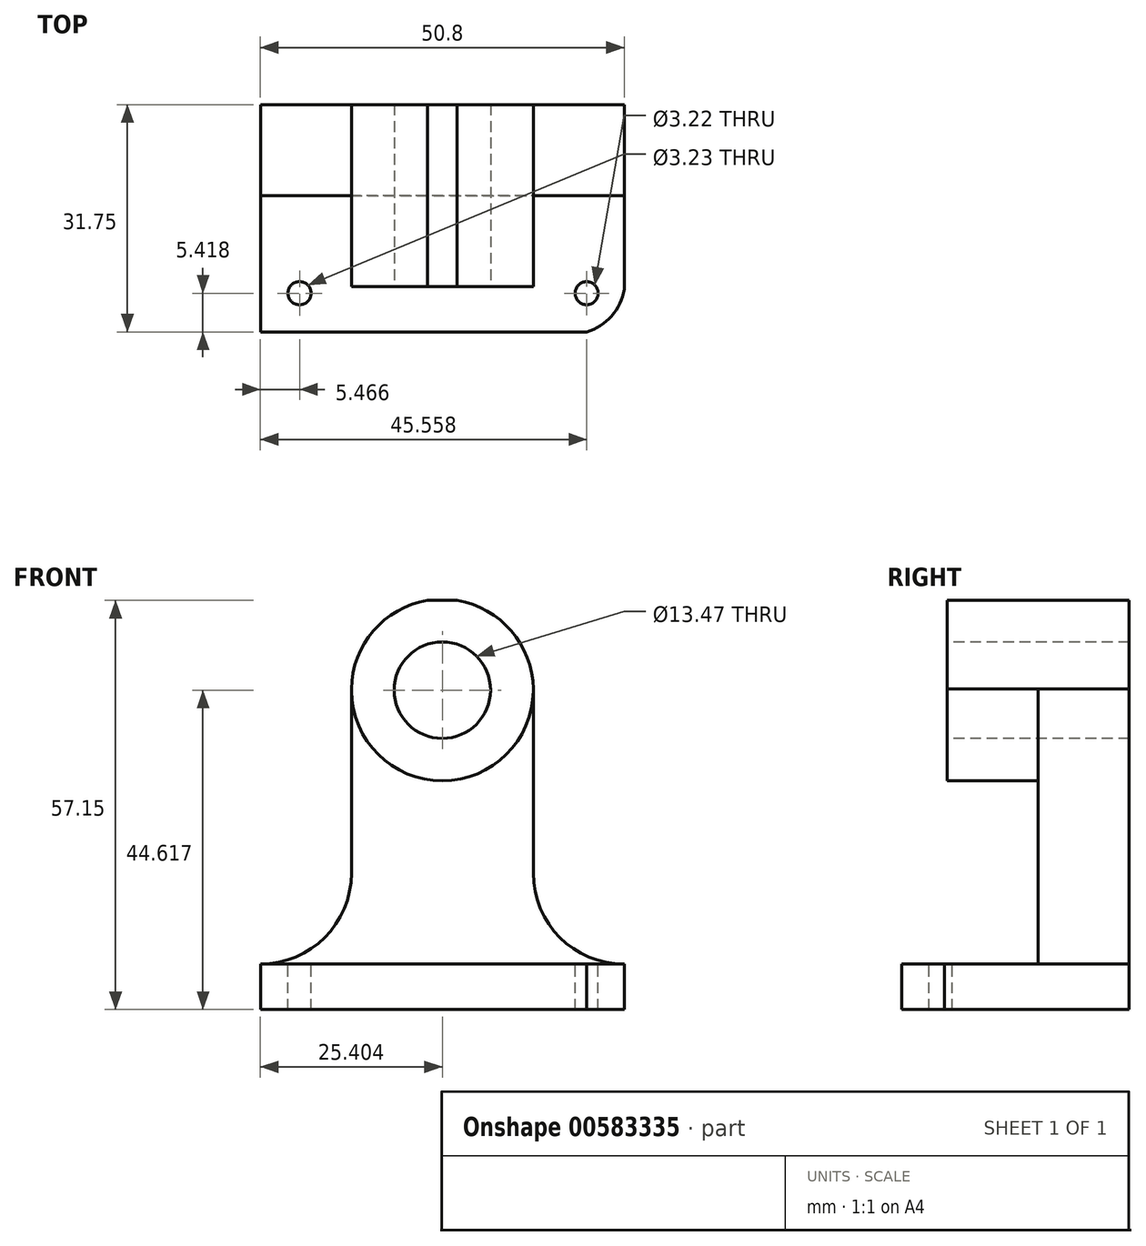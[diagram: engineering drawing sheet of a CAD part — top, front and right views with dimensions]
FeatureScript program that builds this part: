
annotation { "Feature Type Name" : "Feature", "Feature Type Description" : "" }
export const myFeature = defineFeature(function(context is Context, id is Id, definition is map)
    precondition{}
    {
        {
            var Q0;
            Q0=qCreatedBy(makeId("Front.planeOp"),FACE);
            var sketch = newSketch(context, id + "F0", { "sketchPlane" : qUnion([Q0])});
            skLineSegment(sketch, "E0", {"start": v(-69.29, 0) * mm, "end": v(-18.49, 0) * mm});
            skLineSegment(sketch, "E1", {"start": v(-18.49, 0) * mm, "end": v(-18.49, 57.15) * mm});
            skLineSegment(sketch, "E2", {"start": v(-18.49, 57.15) * mm, "end": v(-69.29, 57.15) * mm});
            skLineSegment(sketch, "E3", {"start": v(-69.29, 57.15) * mm, "end": v(-69.29, 0) * mm});
            skSolve(sketch);
        }
        {
            var Q0;
            Q0=makeQuery(id+"F0.imprint","IMPRINT",FACE,{"disambiguationData":[TD([[makeQuery(id+"F0.imprint","IMPRINT",EDGE,{"derivedFrom":sQuery(id+"F0.wireOp",EDGE,"E0")}),1.0]])]});
            extrude(context, id + "F1", {"entities" : qUnion([Q0]), "depth" : 31.75 * mm, "offsetDistance" : 25.4 * mm});
        }
        {
            var Q0;
            Q0=makeQuery(id+"F1.opExtrude","SWEPT_FACE",FACE,{"disambiguationData":[OSD([sQuery(id+"F0.wireOp",EDGE,"E3")])]});
            var sketch = newSketch(context, id + "F2", { "sketchPlane" : qUnion([Q0])});
            skLineSegment(sketch, "E4", {"start": v(31.75, 0) * mm, "end": v(31.75, 6.35) * mm});
            skLineSegment(sketch, "E5", {"start": v(31.75, 6.35) * mm, "end": v(12.7, 6.35) * mm});
            skLineSegment(sketch, "E6", {"start": v(12.7, 6.35) * mm, "end": v(12.7, 31.75) * mm});
            skLineSegment(sketch, "E7", {"start": v(12.7, 31.75) * mm, "end": v(25.4, 31.75) * mm});
            skLineSegment(sketch, "E8", {"start": v(25.4, 31.75) * mm, "end": v(25.4, 57.15) * mm});
            skSolve(sketch);
        }
        {
            var Q0;
            {var subQ1=sQuery(id+"F2.wireOp",EDGE,"E5");Q0=makeQuery(id+"F2.imprint","IMPRINT",FACE,{"disambiguationData":[TD([[makeQuery(id+"F2.imprint","IMPRINT",EDGE,{"derivedFrom":subQ1}),-1.0]])]});}
            extrude(context, id + "F3", {"entities" : qUnion([Q0]), "operationType" : NewBodyOperationType.REMOVE, "oppositeDirection" : true, "depth" : 50.8 * mm, "offsetDistance" : 25.4 * mm});
        }
        {
            var Q0;
            Q0=makeQuery(id+"F3.boolean.opBoolean","COPY",FACE,{"derivedFrom":makeQuery(id+"F3.opExtrude","SWEPT_FACE",FACE,{"disambiguationData":[OSD([sQuery(id+"F2.wireOp",EDGE,"E8")])]})});
            var sketch = newSketch(context, id + "F4", { "sketchPlane" : qUnion([Q0])});
            skLineSegment(sketch, "E9", {"start": v(-69.29, 57.15) * mm, "end": v(-56.59, 57.15) * mm});
            skLineSegment(sketch, "E10", {"start": v(-56.59, 57.15) * mm, "end": v(-56.59, 19.05) * mm});
            skLineSegment(sketch, "E11", {"start": v(-56.59, 19.05) * mm, "end": v(-69.29, 19.05) * mm});
            skLineSegment(sketch, "E12", {"start": v(-18.49, 57.15) * mm, "end": v(-31.19, 57.15) * mm});
            skLineSegment(sketch, "E13", {"start": v(-31.19, 57.15) * mm, "end": v(-31.19, 19.05) * mm});
            skLineSegment(sketch, "E14", {"start": v(-31.19, 19.05) * mm, "end": v(-18.49, 19.05) * mm});
            skSolve(sketch);
        }
        {
            var Q0;
            {var subQ0=sQuery(id+"F4.wireOp",EDGE,"E12");Q0=makeQuery(id+"F4.imprint","IMPRINT",FACE,{"disambiguationData":[TD([[makeQuery(id+"F4.imprint","IMPRINT",EDGE,{"derivedFrom":subQ0}),1.0]])]});}
            var Q1;
            {var subQ0=sQuery(id+"F4.wireOp",EDGE,"E9");Q1=makeQuery(id+"F4.imprint","IMPRINT",FACE,{"disambiguationData":[TD([[makeQuery(id+"F4.imprint","IMPRINT",EDGE,{"derivedFrom":subQ0}),1.0]])]});}
            extrude(context, id + "F5", {"entities" : qUnion([Q0, Q1]), "operationType" : NewBodyOperationType.REMOVE, "oppositeDirection" : true, "depth" : 25.4 * mm, "offsetDistance" : 25.4 * mm});
        }
        {
            var Q0;
            Q0=makeQuery(id+"F3.boolean.opBoolean","COPY",FACE,{"derivedFrom":makeQuery(id+"F3.opExtrude","SWEPT_FACE",FACE,{"disambiguationData":[OSD([sQuery(id+"F2.wireOp",EDGE,"E6")])]})});
            var sketch = newSketch(context, id + "F6", { "sketchPlane" : qUnion([Q0])});
            skLineSegment(sketch, "E15", {"start": v(-56.59, 31.75) * mm, "end": v(-56.59, 19.05) * mm});
            skLineSegment(sketch, "E16", {"start": v(-56.59, 19.05) * mm, "end": v(-69.29, 19.05) * mm});
            skLineSegment(sketch, "E17", {"start": v(-31.19, 31.75) * mm, "end": v(-31.19, 19.05) * mm});
            skLineSegment(sketch, "E18", {"start": v(-31.19, 19.05) * mm, "end": v(-18.49, 19.05) * mm});
            skSolve(sketch);
        }
        {
            var Q0;
            Q0=makeQuery(id+"F6.imprint","IMPRINT",FACE,{"disambiguationData":[TD([[makeQuery(id+"F6.imprint","IMPRINT",EDGE,{"derivedFrom":sQuery(id+"F6.wireOp",EDGE,"E15")}),-1.0]])]});
            var Q1;
            Q1=makeQuery(id+"F6.imprint","IMPRINT",FACE,{"disambiguationData":[TD([[makeQuery(id+"F6.imprint","IMPRINT",EDGE,{"derivedFrom":sQuery(id+"F6.wireOp",EDGE,"E17")}),1.0]])]});
            extrude(context, id + "F7", {"entities" : qUnion([Q0, Q1]), "operationType" : NewBodyOperationType.REMOVE, "oppositeDirection" : true, "depth" : 25.4 * mm, "offsetDistance" : 25.4 * mm});
        }
        {
            var Q0;
            Q0=makeQuery(id+"F3.boolean.opBoolean","COPY",FACE,{"derivedFrom":makeQuery(id+"F3.opExtrude","SWEPT_FACE",FACE,{"disambiguationData":[OSD([sQuery(id+"F2.wireOp",EDGE,"E6")])]})});
            var sketch = newSketch(context, id + "F8", { "sketchPlane" : qUnion([Q0])});
            skArc(sketch, "E19", {"start": v(-69.29, 6.35) * mm, "mid": v(-60.3, 10.07) * mm, "end": v(-56.59, 19.05) * mm});
            skArc(sketch, "E20", {"start": v(-31.19, 19.05) * mm, "mid": v(-27.47, 10.07) * mm, "end": v(-18.49, 6.35) * mm});
            skSolve(sketch);
        }
        {
            var Q0;
            Q0=makeQuery(id+"F8.imprint","IMPRINT",FACE,{"disambiguationData":[TD([[makeQuery(id+"F8.imprint","IMPRINT",EDGE,{"derivedFrom":sQuery(id+"F8.wireOp",EDGE,"E19")}),1.0]])]});
            var Q1;
            Q1=makeQuery(id+"F8.imprint","IMPRINT",FACE,{"disambiguationData":[TD([[makeQuery(id+"F8.imprint","IMPRINT",EDGE,{"derivedFrom":sQuery(id+"F8.wireOp",EDGE,"E20")}),1.0]])]});
            extrude(context, id + "F9", {"entities" : qUnion([Q0, Q1]), "operationType" : NewBodyOperationType.REMOVE, "oppositeDirection" : true, "depth" : 25.4 * mm, "offsetDistance" : 25.4 * mm});
        }
        {
            var Q0;
            Q0=makeQuery(id+"F3.boolean.opBoolean","COPY",FACE,{"derivedFrom":makeQuery(id+"F3.opExtrude","SWEPT_FACE",FACE,{"disambiguationData":[OSD([sQuery(id+"F2.wireOp",EDGE,"E8")])]})});
            var sketch = newSketch(context, id + "F10", { "sketchPlane" : qUnion([Q0])});
            skArc(sketch, "E21", {"start": v(-31.19, 44.45) * mm, "mid": v(-43.89, 57.32) * mm, "end": v(-56.59, 44.45) * mm});
            skArc(sketch, "E22", {"start": v(-56.59, 44.45) * mm, "mid": v(-43.89, 32) * mm, "end": v(-31.19, 44.45) * mm});
            skSolve(sketch);
        }
        {
            var Q0;
            {var subQ0=sQuery(id+"F10.wireOp",EDGE,"E21");var subQ3=makeQuery(id+"F5.boolean.opBoolean","COPY",EDGE,{"derivedFrom":makeQuery(id+"F5.opExtrude","CAP_EDGE",EDGE,{"disambiguationData":[OSD([sQuery(id+"F4.wireOp",EDGE,"E10")])],"isStart":true})});var subQ4=makeQuery(id+"F10.imprint","INTERSECT",VERTEX,{"derivedFrom":[subQ3,subQ0]});Q0=makeQuery(id+"F10.imprint","IMPRINT",FACE,{"disambiguationData":[TD([[makeQuery(id+"F10.imprint","IMPRINT",EDGE,{"disambiguationData":[TD([[subQ4,1.0]])],"derivedFrom":subQ0}),-1.0]])]});}
            var Q1;
            {var subQ0=sQuery(id+"F10.wireOp",EDGE,"E21");var subQ1=makeQuery(id+"F5.boolean.opBoolean","COPY",EDGE,{"derivedFrom":makeQuery(id+"F5.opExtrude","CAP_EDGE",EDGE,{"disambiguationData":[OSD([sQuery(id+"F4.wireOp",EDGE,"E13")])],"isStart":true})});var subQ2=makeQuery(id+"F10.imprint","INTERSECT",VERTEX,{"derivedFrom":[subQ1,subQ0]});Q1=makeQuery(id+"F10.imprint","IMPRINT",FACE,{"disambiguationData":[TD([[makeQuery(id+"F10.imprint","IMPRINT",EDGE,{"disambiguationData":[TD([[subQ2,-1.0]])],"derivedFrom":subQ0}),-1.0]])]});}
            extrude(context, id + "F11", {"entities" : qUnion([Q0, Q1]), "operationType" : NewBodyOperationType.REMOVE, "oppositeDirection" : true, "depth" : 25.4 * mm, "offsetDistance" : 25.4 * mm});
        }
        {
            var Q0;
            Q0=makeQuery(id+"F3.boolean.opBoolean","COPY",FACE,{"derivedFrom":makeQuery(id+"F3.opExtrude","SWEPT_FACE",FACE,{"disambiguationData":[OSD([sQuery(id+"F2.wireOp",EDGE,"E8")])]})});
            var sketch = newSketch(context, id + "F12", { "sketchPlane" : qUnion([Q0])});
            skArc(sketch, "E23", {"start": v(-56.59, 44.78) * mm, "mid": v(-43.89, 31.96) * mm, "end": v(-31.19, 44.78) * mm});
            skSolve(sketch);
        }
        {
            var Q0;
            {var subQ5=makeQuery(id+"F3.boolean.opBoolean","COPY",EDGE,{"derivedFrom":makeQuery(id+"F3.opExtrude","SWEPT_EDGE",EDGE,{"disambiguationData":[OSD([sQuery(id+"F2.wireOp",EDGE,"E7"),sQuery(id+"F2.wireOp",EDGE,"E8")])]})});Q0=makeQuery(id+"F12.imprint","IMPRINT",FACE,{"disambiguationData":[TD([[makeQuery(id+"F12.imprint","IMPRINT",EDGE,{"derivedFrom":subQ5}),-1.0]])]});}
            extrude(context, id + "F13", {"entities" : qUnion([Q0]), "operationType" : NewBodyOperationType.REMOVE, "oppositeDirection" : true, "depth" : 12.7 * mm, "offsetDistance" : 25.4 * mm});
        }
        {
            var Q0;
            Q0=makeQuery(id+"F3.boolean.opBoolean","COPY",FACE,{"derivedFrom":makeQuery(id+"F3.opExtrude","SWEPT_FACE",FACE,{"disambiguationData":[OSD([sQuery(id+"F2.wireOp",EDGE,"E8")])]})});
            var sketch = newSketch(context, id + "F14", { "sketchPlane" : qUnion([Q0])});
            skCircle(sketch, "E24", {"center": v(-43.89, 44.62) * mm, "radius": 6.73 * mm});
            skSolve(sketch);
        }
        {
            var Q0;
            Q0=makeQuery(id+"F14.imprint","IMPRINT",FACE,{"disambiguationData":[TD([[makeQuery(id+"F14.imprint","IMPRINT",EDGE,{"derivedFrom":sQuery(id+"F14.wireOp",EDGE,"E24")}),1.0]])]});
            extrude(context, id + "F15", {"entities" : qUnion([Q0]), "operationType" : NewBodyOperationType.REMOVE, "oppositeDirection" : true, "depth" : 25.4 * mm, "offsetDistance" : 25.4 * mm});
        }
        {
            var Q0;
            Q0=makeQuery(id+"F3.boolean.opBoolean","COPY",FACE,{"derivedFrom":makeQuery(id+"F3.opExtrude","SWEPT_FACE",FACE,{"disambiguationData":[OSD([sQuery(id+"F2.wireOp",EDGE,"E5")])]})});
            var sketch = newSketch(context, id + "F16", { "sketchPlane" : qUnion([Q0])});
            skArc(sketch, "E25", {"start": v(-69.29, -25.77) * mm, "mid": v(-67.59, -30.33) * mm, "end": v(-62.93, -31.75) * mm});
            skArc(sketch, "E26", {"start": v(-23.73, -31.75) * mm, "mid": v(-20.23, -29.52) * mm, "end": v(-18.49, -25.77) * mm});
            skSolve(sketch);
        }
        {
            var Q0;
            {var subQ0=sQuery(id+"F16.wireOp",EDGE,"E25");var subQ1=sQuery(id+"F2.wireOp",EDGE,"E5");var subQ2=makeQuery(id+"F3.boolean.opBoolean","COPY",EDGE,{"derivedFrom":makeQuery(id+"F3.opExtrude","CAP_EDGE",EDGE,{"disambiguationData":[OSD([subQ1])],"isStart":true})});var subQ3=makeQuery(id+"F16.imprint","INTERSECT",VERTEX,{"disambiguationData":[OD(1.0)],"derivedFrom":[subQ2,subQ0]});Q0=makeQuery(id+"F16.imprint","IMPRINT",FACE,{"disambiguationData":[TD([[makeQuery(id+"F16.imprint","IMPRINT",EDGE,{"disambiguationData":[TD([[subQ3,-1.0]])],"derivedFrom":subQ0}),-1.0]])]});}
            var Q1;
            {var subQ0=sQuery(id+"F16.wireOp",EDGE,"E26");Q1=makeQuery(id+"F16.imprint","IMPRINT",FACE,{"disambiguationData":[TD([[makeQuery(id+"F16.imprint","IMPRINT",EDGE,{"derivedFrom":subQ0}),-1.0]])]});}
            extrude(context, id + "F17", {"entities" : qUnion([Q0, Q1]), "operationType" : NewBodyOperationType.REMOVE, "oppositeDirection" : true, "depth" : 25.4 * mm, "offsetDistance" : 25.4 * mm});
        }
        {
            var Q0;
            Q0=makeQuery(id+"F3.boolean.opBoolean","COPY",FACE,{"derivedFrom":makeQuery(id+"F3.opExtrude","SWEPT_FACE",FACE,{"disambiguationData":[OSD([sQuery(id+"F2.wireOp",EDGE,"E5")])]})});
            var sketch = newSketch(context, id + "F18", { "sketchPlane" : qUnion([Q0])});
            skCircle(sketch, "E27", {"center": v(-63.82, -26.33) * mm, "radius": 1.61 * mm});
            skCircle(sketch, "E28", {"center": v(-23.73, -26.33) * mm, "radius": 1.61 * mm});
            skSolve(sketch);
        }
        {
            var Q0;
            Q0=makeQuery(id+"F18.imprint","IMPRINT",FACE,{"disambiguationData":[TD([[makeQuery(id+"F18.imprint","IMPRINT",EDGE,{"derivedFrom":sQuery(id+"F18.wireOp",EDGE,"E27")}),1.0]])]});
            var Q1;
            Q1=makeQuery(id+"F18.imprint","IMPRINT",FACE,{"disambiguationData":[TD([[makeQuery(id+"F18.imprint","IMPRINT",EDGE,{"derivedFrom":sQuery(id+"F18.wireOp",EDGE,"E28")}),1.0]])]});
            extrude(context, id + "F19", {"entities" : qUnion([Q0, Q1]), "operationType" : NewBodyOperationType.REMOVE, "oppositeDirection" : true, "depth" : 25.4 * mm, "offsetDistance" : 25.4 * mm});
        }
    });
